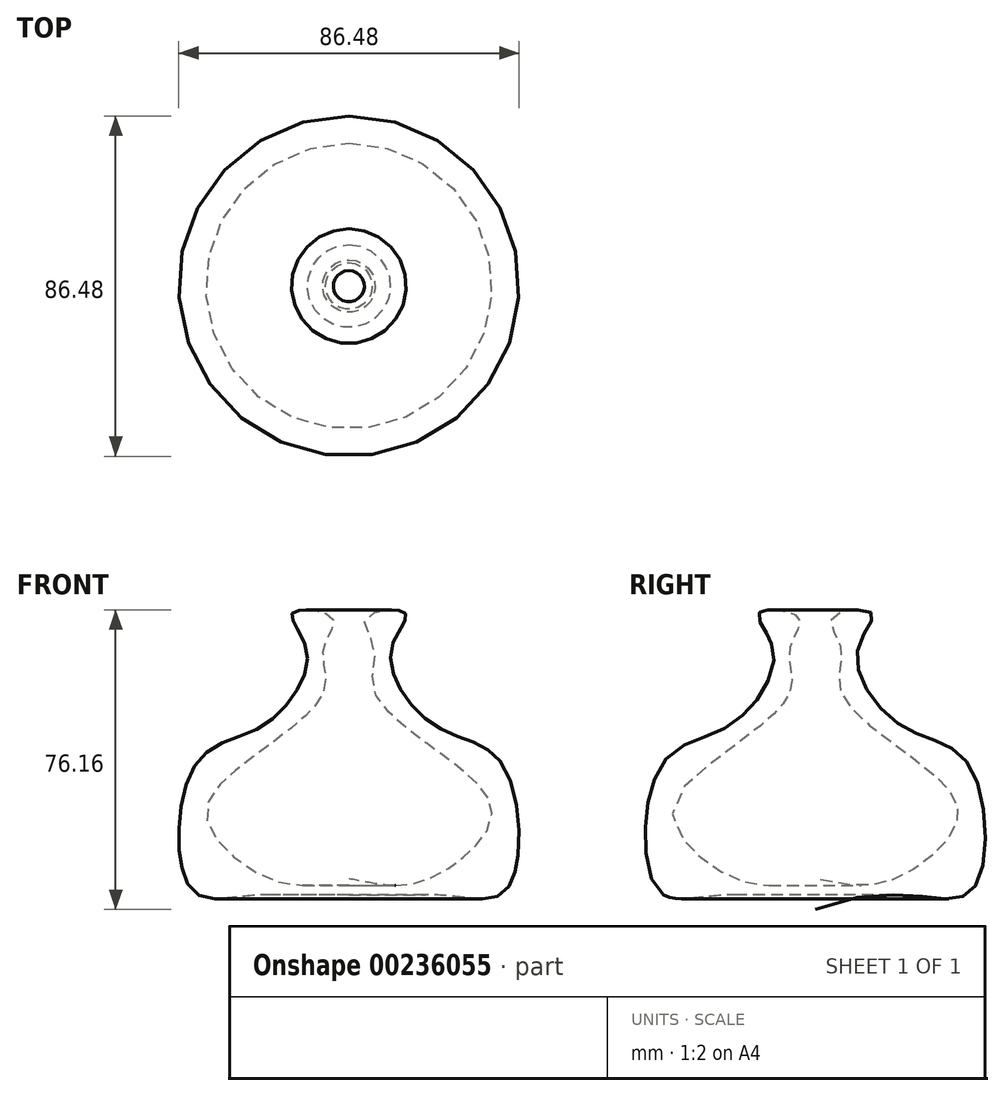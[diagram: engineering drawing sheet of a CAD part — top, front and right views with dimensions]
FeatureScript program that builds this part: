
annotation { "Feature Type Name" : "Feature", "Feature Type Description" : "" }
export const myFeature = defineFeature(function(context is Context, id is Id, definition is map)
    precondition{}
    {
        {
            var Q0;
            Q0=qCreatedBy(makeId("Right.planeOp"),FACE);
            var sketch = newSketch(context, id + "F0", { "sketchPlane" : qUnion([Q0])});
            skFitSpline(sketch, "E0", {"points": [v(0, 0) * mm, v(39.92, 4.93) * mm, v(39.04, 36.82) * mm, v(21.87, 46.72) * mm, v(10.72, 66.1) * mm, v(14.27, 75.34) * mm, v(4.33, 74.23) * mm, v(6.53, 66.3) * mm, v(6.48, 55.18) * mm, v(30.85, 33.65) * mm, v(35.73, 21.5) * mm, v(17.97, 7) * mm, v(0, 7.83) * mm], "startDerivative": vector(546.57, 214.58) * mm, "endDerivative": vector(-222.49, 40.92) * mm});
            skLineSegment(sketch, "E1", {"start": v(0, 7.83) * mm, "end": v(0, 0) * mm});
            skPoint(sketch, "E2", {"position": v(11.6, 58.93) * mm});
            skSolve(sketch);
        }
        {
            var Q0;
            Q0=makeQuery(id+"F0.imprint","IMPRINT",FACE,{"disambiguationData":[TD([[makeQuery(id+"F0.imprint","IMPRINT",EDGE,{"derivedFrom":sQuery(id+"F0.wireOp",EDGE,"E0")}),1.0]])]});
            var Q1;
            Q1=sQuery(id+"F0.wireOp",EDGE,"E1");
            revolve(context, id + "F1", {"entities" : qUnion([Q0]), "axis" : qUnion([Q1]), "revolveType" : RevolveType.FULL});
        }
    });
